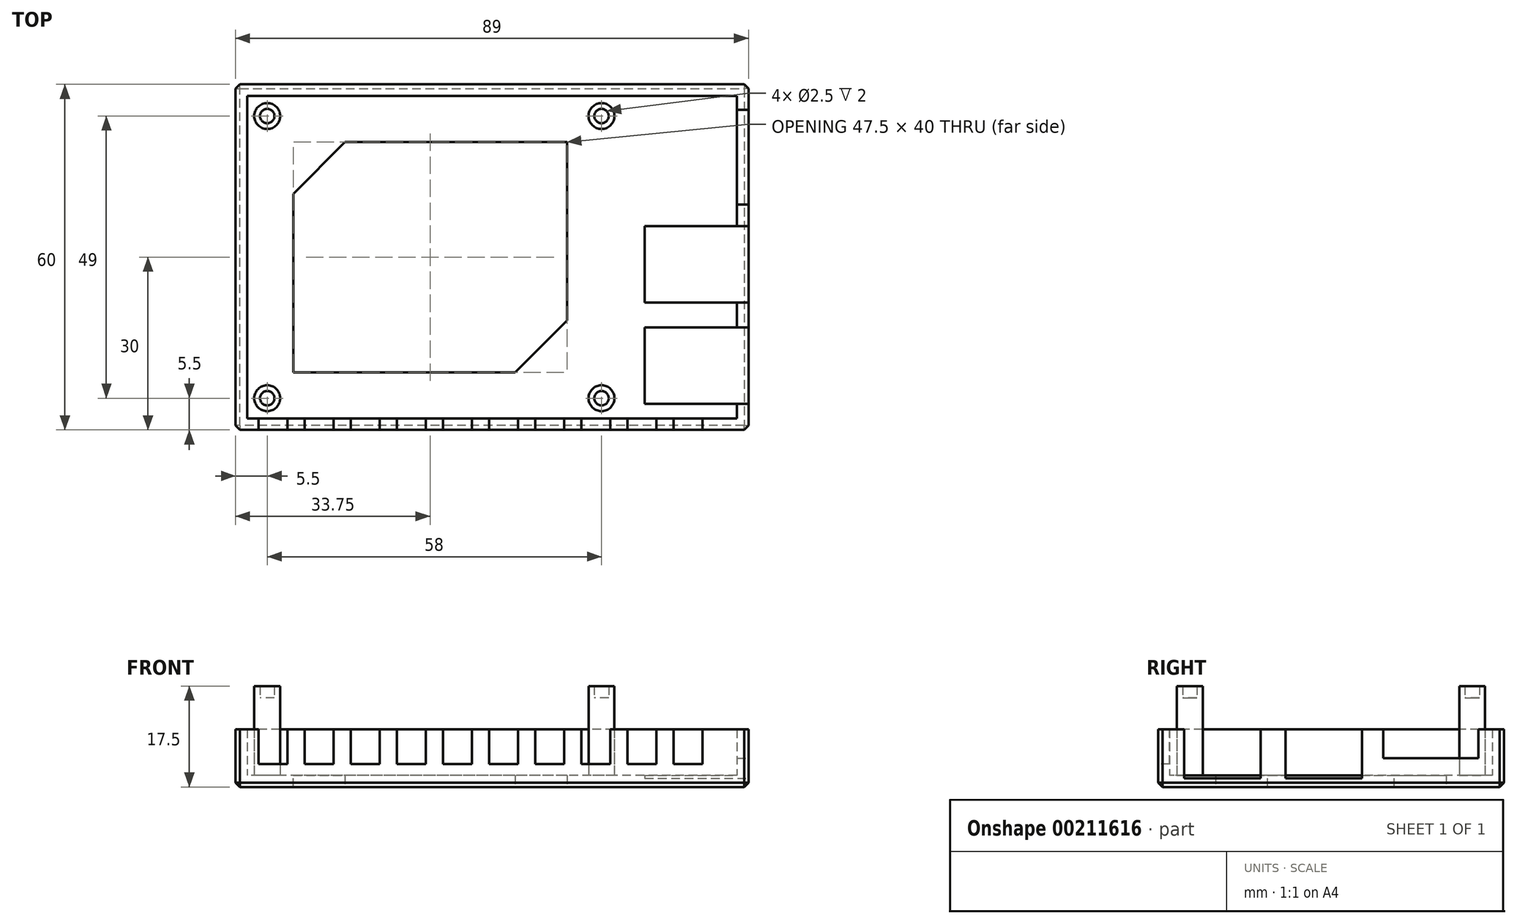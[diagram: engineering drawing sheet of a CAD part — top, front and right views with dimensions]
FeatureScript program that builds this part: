
annotation { "Feature Type Name" : "Feature", "Feature Type Description" : "" }
export const myFeature = defineFeature(function(context is Context, id is Id, definition is map)
    precondition{}
    {
        {
            var Q0;
            Q0=qCreatedBy(makeId("Top.planeOp"),FACE);
            var sketch = newSketch(context, id + "F0", { "sketchPlane" : qUnion([Q0])});
            skLineSegment(sketch, "E0.bottom", {"start": v(42.5, 28) * mm, "end": v(-42.5, 28) * mm});
            skLineSegment(sketch, "E0.top", {"start": v(42.5, -28) * mm, "end": v(-42.5, -28) * mm});
            skLineSegment(sketch, "E0.left", {"start": v(42.5, 28) * mm, "end": v(42.5, -28) * mm});
            skLineSegment(sketch, "E0.right", {"start": v(-42.5, 28) * mm, "end": v(-42.5, -28) * mm});
            skPoint(sketch, "E0.middle", {"position": v(0, 0) * mm});
            skLineSegment(sketch, "E1.0", {"start": v(44.5, 30) * mm, "end": v(-44.5, 30) * mm});
            skLineSegment(sketch, "E1.1", {"start": v(44.5, 30) * mm, "end": v(44.5, -30) * mm});
            skLineSegment(sketch, "E1.2", {"start": v(44.5, -30) * mm, "end": v(-44.5, -30) * mm});
            skLineSegment(sketch, "E1.3", {"start": v(-44.5, 30) * mm, "end": v(-44.5, -30) * mm});
            skSolve(sketch);
        }
        {
            var Q0;
            Q0 = qSketchRegion(id + "F0", true);
            extrude(context, id + "F1", {"entities" : qUnion([Q0]), "depth" : 10 * mm});
        }
        {
            var Q0;
            Q0=makeQuery(id+"F0.imprint","IMPRINT",FACE,{"disambiguationData":[TD([[makeQuery(id+"F0.imprint","IMPRINT",EDGE,{"derivedFrom":sQuery(id+"F0.wireOp",EDGE,"E0.bottom")}),1.0]])]});
            extrude(context, id + "F2", {"entities" : qUnion([Q0]), "operationType" : NewBodyOperationType.ADD, "depth" : 2 * mm});
        }
        {
            var Q0;
            Q0=makeQuery(id+"F1.opExtrude","SWEPT_FACE",FACE,{"disambiguationData":[OSD([sQuery(id+"F0.wireOp",EDGE,"E1.1")])]});
            var sketch = newSketch(context, id + "F3", { "sketchPlane" : qUnion([Q0])});
            skLineSegment(sketch, "E2.bottom", {"start": v(-25.5, 10) * mm, "end": v(-12.2, 10) * mm});
            skLineSegment(sketch, "E2.top", {"start": v(-25.5, 1.5) * mm, "end": v(-12.2, 1.5) * mm});
            skLineSegment(sketch, "E2.left", {"start": v(-25.5, 10) * mm, "end": v(-25.5, 1.5) * mm});
            skLineSegment(sketch, "E2.right", {"start": v(-12.2, 10) * mm, "end": v(-12.2, 1.5) * mm});
            skLineSegment(sketch, "E3.bottom", {"start": v(-7.9, 10) * mm, "end": v(5.4, 10) * mm});
            skLineSegment(sketch, "E3.top", {"start": v(-7.9, 1.5) * mm, "end": v(5.4, 1.5) * mm});
            skLineSegment(sketch, "E3.left", {"start": v(-7.9, 10) * mm, "end": v(-7.9, 1.5) * mm});
            skLineSegment(sketch, "E3.right", {"start": v(5.4, 10) * mm, "end": v(5.4, 1.5) * mm});
            skLineSegment(sketch, "E4.bottom", {"start": v(9.1, 10) * mm, "end": v(25.6, 10) * mm});
            skLineSegment(sketch, "E4.top", {"start": v(9.1, 5) * mm, "end": v(25.6, 5) * mm});
            skLineSegment(sketch, "E4.left", {"start": v(9.1, 10) * mm, "end": v(9.1, 5) * mm});
            skLineSegment(sketch, "E4.right", {"start": v(25.6, 10) * mm, "end": v(25.6, 5) * mm});
            skPoint(sketch, "E5.middle", {"position": v(17.35, 7.5) * mm});
            skSolve(sketch);
        }
        {
            var Q0;
            Q0 = qSketchRegion(id + "F3", true);
            extrude(context, id + "F4", {"entities" : qUnion([Q0]), "operationType" : NewBodyOperationType.REMOVE, "oppositeDirection" : true, "depth" : 18 * mm});
        }
        {
            var Q0;
            {var subQ0=sQuery(id+"F0.wireOp",EDGE,"E0.right");var subQ1=sQuery(id+"F0.wireOp",EDGE,"E0.left");var subQ2=sQuery(id+"F0.wireOp",EDGE,"E0.top");var subQ3=sQuery(id+"F0.wireOp",EDGE,"E0.bottom");Q0=makeQuery(id+"F2.boolean.opBoolean","MERGE",FACE,{"derivedFrom":[makeQuery(id+"F1.opExtrude","CAP_FACE",FACE,{"disambiguationData":[OSD([subQ3,subQ2,subQ1,subQ0,sQuery(id+"F0.wireOp",EDGE,"E1.0"),sQuery(id+"F0.wireOp",EDGE,"E1.1"),sQuery(id+"F0.wireOp",EDGE,"E1.2"),sQuery(id+"F0.wireOp",EDGE,"E1.3")])],"isStart":true}),makeQuery(id+"F2.opExtrude","CAP_FACE",FACE,{"disambiguationData":[OSD([subQ3,subQ2,subQ1,subQ0])],"isStart":true})]});}
            var Q1;
            Q1=makeQuery(id+"F1.opExtrude","SWEPT_EDGE",EDGE,{"disambiguationData":[OSD([sQuery(id+"F0.wireOp",EDGE,"E1.1"),sQuery(id+"F0.wireOp",EDGE,"E1.2")])]});
            var Q2;
            Q2=makeQuery(id+"F1.opExtrude","SWEPT_EDGE",EDGE,{"disambiguationData":[OSD([sQuery(id+"F0.wireOp",EDGE,"E1.2"),sQuery(id+"F0.wireOp",EDGE,"E1.3")])]});
            var Q3;
            Q3=makeQuery(id+"F1.opExtrude","SWEPT_EDGE",EDGE,{"disambiguationData":[OSD([sQuery(id+"F0.wireOp",EDGE,"E1.0"),sQuery(id+"F0.wireOp",EDGE,"E1.3")])]});
            var Q4;
            Q4=makeQuery(id+"F1.opExtrude","SWEPT_EDGE",EDGE,{"disambiguationData":[OSD([sQuery(id+"F0.wireOp",EDGE,"E1.0"),sQuery(id+"F0.wireOp",EDGE,"E1.1")])]});
            chamfer(context, id + "F5", {"entities" : qUnion([Q0, Q1, Q2, Q3, Q4]), "width" : 0.75 * mm, "tangentPropagation" : true});
        }
        {
            var Q0;
            Q0=makeQuery(id+"F0.imprint","IMPRINT",FACE,{"disambiguationData":[TD([[makeQuery(id+"F0.imprint","IMPRINT",EDGE,{"derivedFrom":sQuery(id+"F0.wireOp",EDGE,"E0.bottom")}),1.0]])]});
            var sketch = newSketch(context, id + "F6", { "sketchPlane" : qUnion([Q0])});
            skCircle(sketch, "E6", {"center": v(-39, -24.5) * mm, "radius": 1.25 * mm});
            skCircle(sketch, "E7.1.0.0", {"center": v(19, -24.5) * mm, "radius": 1.25 * mm});
            skLineSegment(sketch, "E7.direction1", {"start": v(-39, -24.5) * mm, "end": v(19, -24.5) * mm, "construction": true});
            skCircle(sketch, "E8.0", {"center": v(-39, -24.5) * mm, "radius": 2.25 * mm});
            skCircle(sketch, "E9.0", {"center": v(19, -24.5) * mm, "radius": 2.25 * mm});
            skCircle(sketch, "E10.MirrorC", {"center": v(19, 24.5) * mm, "radius": 2.25 * mm});
            skCircle(sketch, "E11.MirrorC", {"center": v(-39, 24.5) * mm, "radius": 1.25 * mm});
            skCircle(sketch, "E12.MirrorC", {"center": v(-39, 24.5) * mm, "radius": 2.25 * mm});
            skCircle(sketch, "E13.MirrorC", {"center": v(19, 24.5) * mm, "radius": 1.25 * mm});
            skSolve(sketch);
        }
        {
            var Q0;
            Q0 = qSketchRegion(id + "F6", true);
            extrude(context, id + "F7", {"entities" : qUnion([Q0]), "operationType" : NewBodyOperationType.ADD, "depth" : 17.5 * mm});
        }
        {
            var Q0;
            Q0=makeQuery(id+"F7.boolean.opBoolean","SPLIT",FACE,{"disambiguationData":[TD([makeQuery(id+"F7.opExtrude","SWEPT_FACE",FACE,{"disambiguationData":[OSD([sQuery(id+"F6.wireOp",EDGE,"E11.MirrorC")])]})])],"derivedFrom":makeQuery(id+"F2.opExtrude","CAP_FACE",FACE,{"disambiguationData":[OSD([sQuery(id+"F0.wireOp",EDGE,"E0.bottom"),sQuery(id+"F0.wireOp",EDGE,"E0.top"),sQuery(id+"F0.wireOp",EDGE,"E0.left"),sQuery(id+"F0.wireOp",EDGE,"E0.right")])],"isStart":false})});
            var Q1;
            Q1=makeQuery(id+"F7.boolean.opBoolean","SPLIT",FACE,{"disambiguationData":[TD([makeQuery(id+"F7.opExtrude","SWEPT_FACE",FACE,{"disambiguationData":[OSD([sQuery(id+"F6.wireOp",EDGE,"E6")])]})])],"derivedFrom":makeQuery(id+"F2.opExtrude","CAP_FACE",FACE,{"disambiguationData":[OSD([sQuery(id+"F0.wireOp",EDGE,"E0.bottom"),sQuery(id+"F0.wireOp",EDGE,"E0.top"),sQuery(id+"F0.wireOp",EDGE,"E0.left"),sQuery(id+"F0.wireOp",EDGE,"E0.right")])],"isStart":false})});
            var Q2;
            Q2=makeQuery(id+"F7.boolean.opBoolean","SPLIT",FACE,{"disambiguationData":[TD([makeQuery(id+"F7.opExtrude","SWEPT_FACE",FACE,{"disambiguationData":[OSD([sQuery(id+"F6.wireOp",EDGE,"E13.MirrorC")])]})])],"derivedFrom":makeQuery(id+"F2.opExtrude","CAP_FACE",FACE,{"disambiguationData":[OSD([sQuery(id+"F0.wireOp",EDGE,"E0.bottom"),sQuery(id+"F0.wireOp",EDGE,"E0.top"),sQuery(id+"F0.wireOp",EDGE,"E0.left"),sQuery(id+"F0.wireOp",EDGE,"E0.right")])],"isStart":false})});
            var Q3;
            Q3=makeQuery(id+"F7.boolean.opBoolean","SPLIT",FACE,{"disambiguationData":[TD([makeQuery(id+"F7.opExtrude","SWEPT_FACE",FACE,{"disambiguationData":[OSD([sQuery(id+"F6.wireOp",EDGE,"E7.1.0.0")])]})])],"derivedFrom":makeQuery(id+"F2.opExtrude","CAP_FACE",FACE,{"disambiguationData":[OSD([sQuery(id+"F0.wireOp",EDGE,"E0.bottom"),sQuery(id+"F0.wireOp",EDGE,"E0.top"),sQuery(id+"F0.wireOp",EDGE,"E0.left"),sQuery(id+"F0.wireOp",EDGE,"E0.right")])],"isStart":false})});
            extrude(context, id + "F8", {"entities" : qUnion([Q0, Q1, Q2, Q3]), "operationType" : NewBodyOperationType.ADD, "depth" : 13.5 * mm});
        }
        {
            var Q0;
            Q0=makeQuery(id+"F0.imprint","IMPRINT",FACE,{"disambiguationData":[TD([[makeQuery(id+"F0.imprint","IMPRINT",EDGE,{"derivedFrom":sQuery(id+"F0.wireOp",EDGE,"E0.bottom")}),1.0]])]});
            var sketch = newSketch(context, id + "F9", { "sketchPlane" : qUnion([Q0])});
            skLineSegment(sketch, "E14.bottom", {"start": v(-34.5, 20) * mm, "end": v(13, 20) * mm});
            skLineSegment(sketch, "E14.top", {"start": v(-34.5, -20) * mm, "end": v(13, -20) * mm});
            skLineSegment(sketch, "E14.left", {"start": v(-34.5, 20) * mm, "end": v(-34.5, -20) * mm});
            skLineSegment(sketch, "E14.right", {"start": v(13, 20) * mm, "end": v(13, -20) * mm});
            skSolve(sketch);
        }
        {
            var Q0;
            Q0 = qSketchRegion(id + "F9", true);
            extrude(context, id + "F10", {"entities" : qUnion([Q0]), "operationType" : NewBodyOperationType.REMOVE, "depth" : 25 * mm});
        }
        {
            var Q0;
            Q0=makeQuery(id+"F10.boolean.opBoolean","COPY",EDGE,{"derivedFrom":makeQuery(id+"F10.opExtrude","SWEPT_EDGE",EDGE,{"disambiguationData":[OSD([sQuery(id+"F9.wireOp",EDGE,"E14.top"),sQuery(id+"F9.wireOp",EDGE,"E14.right")])]})});
            var Q1;
            Q1=makeQuery(id+"F10.boolean.opBoolean","COPY",EDGE,{"derivedFrom":makeQuery(id+"F10.opExtrude","SWEPT_EDGE",EDGE,{"disambiguationData":[OSD([sQuery(id+"F9.wireOp",EDGE,"E14.bottom"),sQuery(id+"F9.wireOp",EDGE,"E14.left")])]})});
            chamfer(context, id + "F11", {"entities" : qUnion([Q0, Q1]), "width" : 9 * mm, "tangentPropagation" : true});
        }
        {
            var Q0;
            Q0=makeQuery(id+"F1.opExtrude","SWEPT_FACE",FACE,{"disambiguationData":[OSD([sQuery(id+"F0.wireOp",EDGE,"E1.2")])]});
            var sketch = newSketch(context, id + "F12", { "sketchPlane" : qUnion([Q0])});
            skLineSegment(sketch, "E15.bottom", {"start": v(36.5, 4) * mm, "end": v(31.5, 4) * mm});
            skLineSegment(sketch, "E15.top", {"start": v(36.5, 10) * mm, "end": v(31.5, 10) * mm});
            skLineSegment(sketch, "E15.left", {"start": v(36.5, 4) * mm, "end": v(36.5, 10) * mm});
            skLineSegment(sketch, "E15.right", {"start": v(31.5, 4) * mm, "end": v(31.5, 10) * mm});
            skLineSegment(sketch, "E16.1.0.0", {"start": v(23.5, 4) * mm, "end": v(23.5, 10) * mm});
            skLineSegment(sketch, "E16.1.0.1", {"start": v(28.5, 10) * mm, "end": v(23.5, 10) * mm});
            skLineSegment(sketch, "E16.1.0.2", {"start": v(28.5, 4) * mm, "end": v(28.5, 10) * mm});
            skLineSegment(sketch, "E16.1.0.3", {"start": v(28.5, 4) * mm, "end": v(23.5, 4) * mm});
            skLineSegment(sketch, "E16.2.0.0", {"start": v(15.5, 4) * mm, "end": v(15.5, 10) * mm});
            skLineSegment(sketch, "E16.2.0.1", {"start": v(20.5, 10) * mm, "end": v(15.5, 10) * mm});
            skLineSegment(sketch, "E16.2.0.2", {"start": v(20.5, 4) * mm, "end": v(20.5, 10) * mm});
            skLineSegment(sketch, "E16.2.0.3", {"start": v(20.5, 4) * mm, "end": v(15.5, 4) * mm});
            skLineSegment(sketch, "E16.3.0.0", {"start": v(7.5, 4) * mm, "end": v(7.5, 10) * mm});
            skLineSegment(sketch, "E16.3.0.1", {"start": v(12.5, 10) * mm, "end": v(7.5, 10) * mm});
            skLineSegment(sketch, "E16.3.0.2", {"start": v(12.5, 4) * mm, "end": v(12.5, 10) * mm});
            skLineSegment(sketch, "E16.3.0.3", {"start": v(12.5, 4) * mm, "end": v(7.5, 4) * mm});
            skLineSegment(sketch, "E16.4.0.0", {"start": v(-0.5, 4) * mm, "end": v(-0.5, 10) * mm});
            skLineSegment(sketch, "E16.4.0.1", {"start": v(4.5, 10) * mm, "end": v(-0.5, 10) * mm});
            skLineSegment(sketch, "E16.4.0.2", {"start": v(4.5, 4) * mm, "end": v(4.5, 10) * mm});
            skLineSegment(sketch, "E16.4.0.3", {"start": v(4.5, 4) * mm, "end": v(-0.5, 4) * mm});
            skLineSegment(sketch, "E16.5.0.0", {"start": v(-8.5, 4) * mm, "end": v(-8.5, 10) * mm});
            skLineSegment(sketch, "E16.5.0.1", {"start": v(-3.5, 10) * mm, "end": v(-8.5, 10) * mm});
            skLineSegment(sketch, "E16.5.0.2", {"start": v(-3.5, 4) * mm, "end": v(-3.5, 10) * mm});
            skLineSegment(sketch, "E16.5.0.3", {"start": v(-3.5, 4) * mm, "end": v(-8.5, 4) * mm});
            skLineSegment(sketch, "E16.6.0.0", {"start": v(-16.5, 4) * mm, "end": v(-16.5, 10) * mm});
            skLineSegment(sketch, "E16.6.0.1", {"start": v(-11.5, 10) * mm, "end": v(-16.5, 10) * mm});
            skLineSegment(sketch, "E16.6.0.2", {"start": v(-11.5, 4) * mm, "end": v(-11.5, 10) * mm});
            skLineSegment(sketch, "E16.6.0.3", {"start": v(-11.5, 4) * mm, "end": v(-16.5, 4) * mm});
            skLineSegment(sketch, "E16.7.0.0", {"start": v(-24.5, 4) * mm, "end": v(-24.5, 10) * mm});
            skLineSegment(sketch, "E16.7.0.1", {"start": v(-19.5, 10) * mm, "end": v(-24.5, 10) * mm});
            skLineSegment(sketch, "E16.7.0.2", {"start": v(-19.5, 4) * mm, "end": v(-19.5, 10) * mm});
            skLineSegment(sketch, "E16.7.0.3", {"start": v(-19.5, 4) * mm, "end": v(-24.5, 4) * mm});
            skLineSegment(sketch, "E16.8.0.0", {"start": v(-32.5, 4) * mm, "end": v(-32.5, 10) * mm});
            skLineSegment(sketch, "E16.8.0.1", {"start": v(-27.5, 10) * mm, "end": v(-32.5, 10) * mm});
            skLineSegment(sketch, "E16.8.0.2", {"start": v(-27.5, 4) * mm, "end": v(-27.5, 10) * mm});
            skLineSegment(sketch, "E16.8.0.3", {"start": v(-27.5, 4) * mm, "end": v(-32.5, 4) * mm});
            skLineSegment(sketch, "E16.9.0.0", {"start": v(-40.5, 4) * mm, "end": v(-40.5, 10) * mm});
            skLineSegment(sketch, "E16.9.0.1", {"start": v(-35.5, 10) * mm, "end": v(-40.5, 10) * mm});
            skLineSegment(sketch, "E16.9.0.2", {"start": v(-35.5, 4) * mm, "end": v(-35.5, 10) * mm});
            skLineSegment(sketch, "E16.9.0.3", {"start": v(-35.5, 4) * mm, "end": v(-40.5, 4) * mm});
            skLineSegment(sketch, "E16.direction1", {"start": v(31.5, 4) * mm, "end": v(23.5, 4) * mm, "construction": true});
            skSolve(sketch);
        }
        {
            var Q0;
            Q0 = qSketchRegion(id + "F12", true);
            extrude(context, id + "F13", {"entities" : qUnion([Q0]), "operationType" : NewBodyOperationType.REMOVE, "oppositeDirection" : true, "depth" : 2 * mm});
        }
    });
